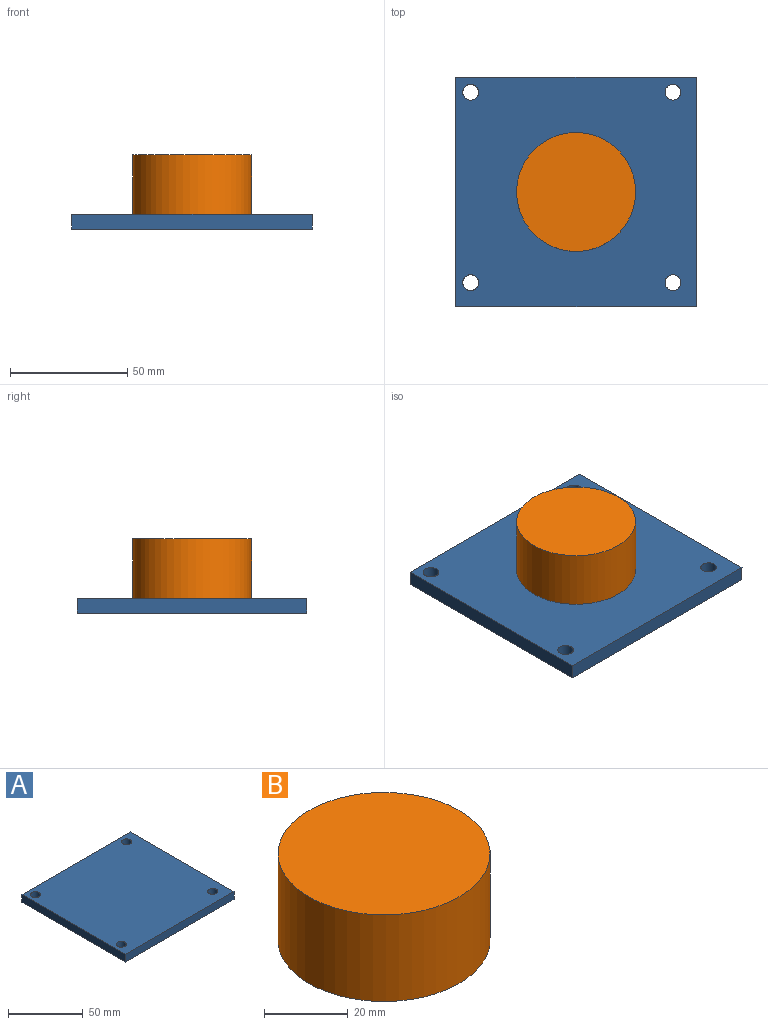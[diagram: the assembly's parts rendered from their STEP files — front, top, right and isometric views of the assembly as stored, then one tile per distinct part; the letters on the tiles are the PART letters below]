
ASSEMBLY  parts=2 mates=1
PART A: 10 faces, bbox 102.6x97.8x6.4 mm
  f0: plane 102.63x6.35mm, normal (0,-1,0), area 651.7mm2, adj f1,f3,f4,f5
  f1: plane 97.83x6.35mm, normal (1,0,0), area 621.2mm2, adj f0,f2,f4,f5
  f2: plane 102.63x6.35mm, normal (0,1,0), area 651.7mm2, adj f1,f3,f4,f5
  f3: plane 97.83x6.35mm, normal (-1,0,0), area 621.2mm2, adj f0,f2,f4,f5
  f4: plane 102.63x97.83mm, normal (0,0,1), area 9896.6mm2, adj f0,f1,f2,f3,f6,f7,f8,f9
  f5: plane 102.63x97.83mm, normal (0,0,-1), area 9896.6mm2, adj f0,f1,f2,f3,f6,f7,f8,f9
  f6: cylinder r=3.38mm len=6.76mm, axis (0,0,-1), area 134.8mm2, adj f4,f5
  f7: cylinder r=3.38mm len=6.76mm, axis (0,0,-1), area 134.8mm2, adj f4,f5
  f8: cylinder r=3.38mm len=6.76mm, axis (0,0,-1), area 134.8mm2, adj f4,f5
  f9: cylinder r=3.38mm len=6.76mm, axis (0,0,-1), area 134.8mm2, adj f4,f5
PART B: 3 faces, bbox 50.8x50.8x25.4 mm
  f0: cylinder r=25.4mm len=50.8mm, axis (0,0,-1), area 4053.7mm2, adj f1,f2
  f1: plane 50.8x50.8mm, normal (0,0,1), area 2026.8mm2, adj f0
  f2: plane 50.8x50.8mm, normal (0,0,-1), area 2026.8mm2, adj f0
PLACE A rot(axis=(0.72,-0.22,-0.65),0deg) t=(-74.65,-33.07,-11.18)mm
PLACE B rot(axis=(0.72,-0.22,-0.65),0deg) t=(-74.63,-33.1,-4.83)mm
MATE fastened A.f4 <-> B.f0  axis (0,0,1) through (-74.63,-33.1,-4.83)mm
